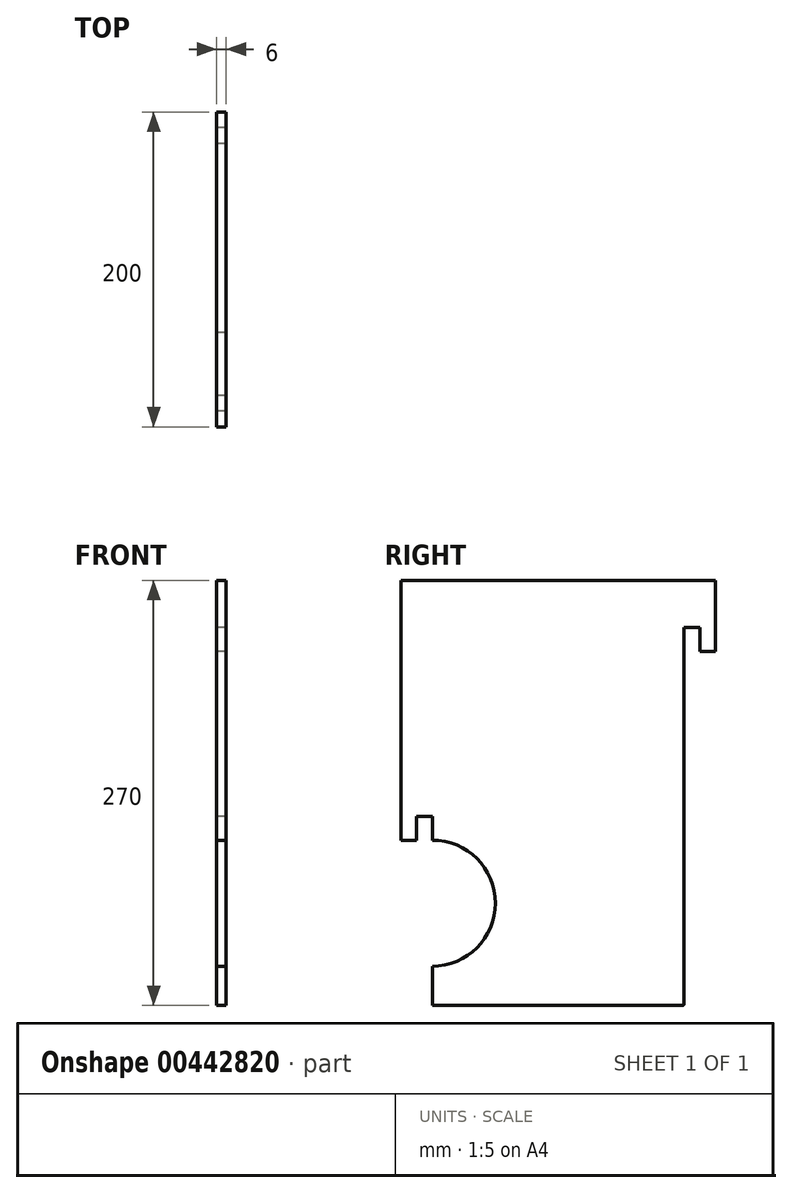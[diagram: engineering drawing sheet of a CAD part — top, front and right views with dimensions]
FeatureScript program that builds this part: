
annotation { "Feature Type Name" : "Feature", "Feature Type Description" : "" }
export const myFeature = defineFeature(function(context is Context, id is Id, definition is map)
    precondition{}
    {
        {
            var Q0;
            Q0=qCreatedBy(makeId("Right.planeOp"),FACE);
            var sketch = newSketch(context, id + "F0", { "sketchPlane" : qUnion([Q0])});
            skLineSegment(sketch, "E0.bottom", {"start": v(-1.27, 0) * mm, "end": v(-160, 0) * mm});
            skLineSegment(sketch, "E0.top", {"start": v(-1.27, 250) * mm, "end": v(-158.73, 250) * mm});
            skLineSegment(sketch, "E0.left", {"start": v(0, 1.27) * mm, "end": v(0, 248.73) * mm});
            skLineSegment(sketch, "E1.trimOffspring", {"start": v(-160, 105) * mm, "end": v(-160, 248.73) * mm});
            skPoint(sketch, "E2.visualSharp", {"position": v(-160, 250) * mm});
            skArc(sketch, "E2.filletArc", {"start": v(-158.73, 250) * mm, "mid": v(-159.63, 249.63) * mm, "end": v(-160, 248.73) * mm});
            skPoint(sketch, "E3.visualSharp", {"position": v(0, 250) * mm});
            skArc(sketch, "E3.filletArc", {"start": v(0, 248.73) * mm, "mid": v(-0.37, 249.63) * mm, "end": v(-1.27, 250) * mm});
            skPoint(sketch, "E4.visualSharp", {"position": v(0, 0) * mm});
            skArc(sketch, "E4.filletArc", {"start": v(-1.27, 0) * mm, "mid": v(-0.37, 0.37) * mm, "end": v(0, 1.27) * mm});
            skLineSegment(sketch, "E5", {"start": v(-160, 0) * mm, "end": v(-160, 25) * mm});
            skArc(sketch, "E6", {"start": v(-160, 25) * mm, "mid": v(-120, 65) * mm, "end": v(-160, 105) * mm});
            skLineSegment(sketch, "E7", {"start": v(-170, 105) * mm, "end": v(-180, 105) * mm});
            skLineSegment(sketch, "E8", {"start": v(-180, 105) * mm, "end": v(-180, 270) * mm});
            skLineSegment(sketch, "E9", {"start": v(-180, 270) * mm, "end": v(20, 270) * mm});
            skLineSegment(sketch, "E10", {"start": v(-170, 105) * mm, "end": v(-170, 120) * mm});
            skLineSegment(sketch, "E11", {"start": v(-170, 120) * mm, "end": v(-160, 120) * mm});
            skLineSegment(sketch, "E12", {"start": v(-160, 105) * mm, "end": v(-160, -34) * mm, "construction": true});
            skLineSegment(sketch, "E13", {"start": v(20, 270) * mm, "end": v(20, 225) * mm});
            skLineSegment(sketch, "E14", {"start": v(20, 225) * mm, "end": v(10, 225) * mm});
            skLineSegment(sketch, "E15", {"start": v(10, 225) * mm, "end": v(10, 240) * mm});
            skLineSegment(sketch, "E16", {"start": v(10, 240) * mm, "end": v(0, 240) * mm});
            skSolve(sketch);
        }
        {
            var Q0;
            Q0=qSketchRegion(id+"F0",true);
            extrude(context, id + "F1", {"entities" : qUnion([Q0]), "depth" : 6 * mm, "offsetDistance" : 25 * mm});
        }
    });
